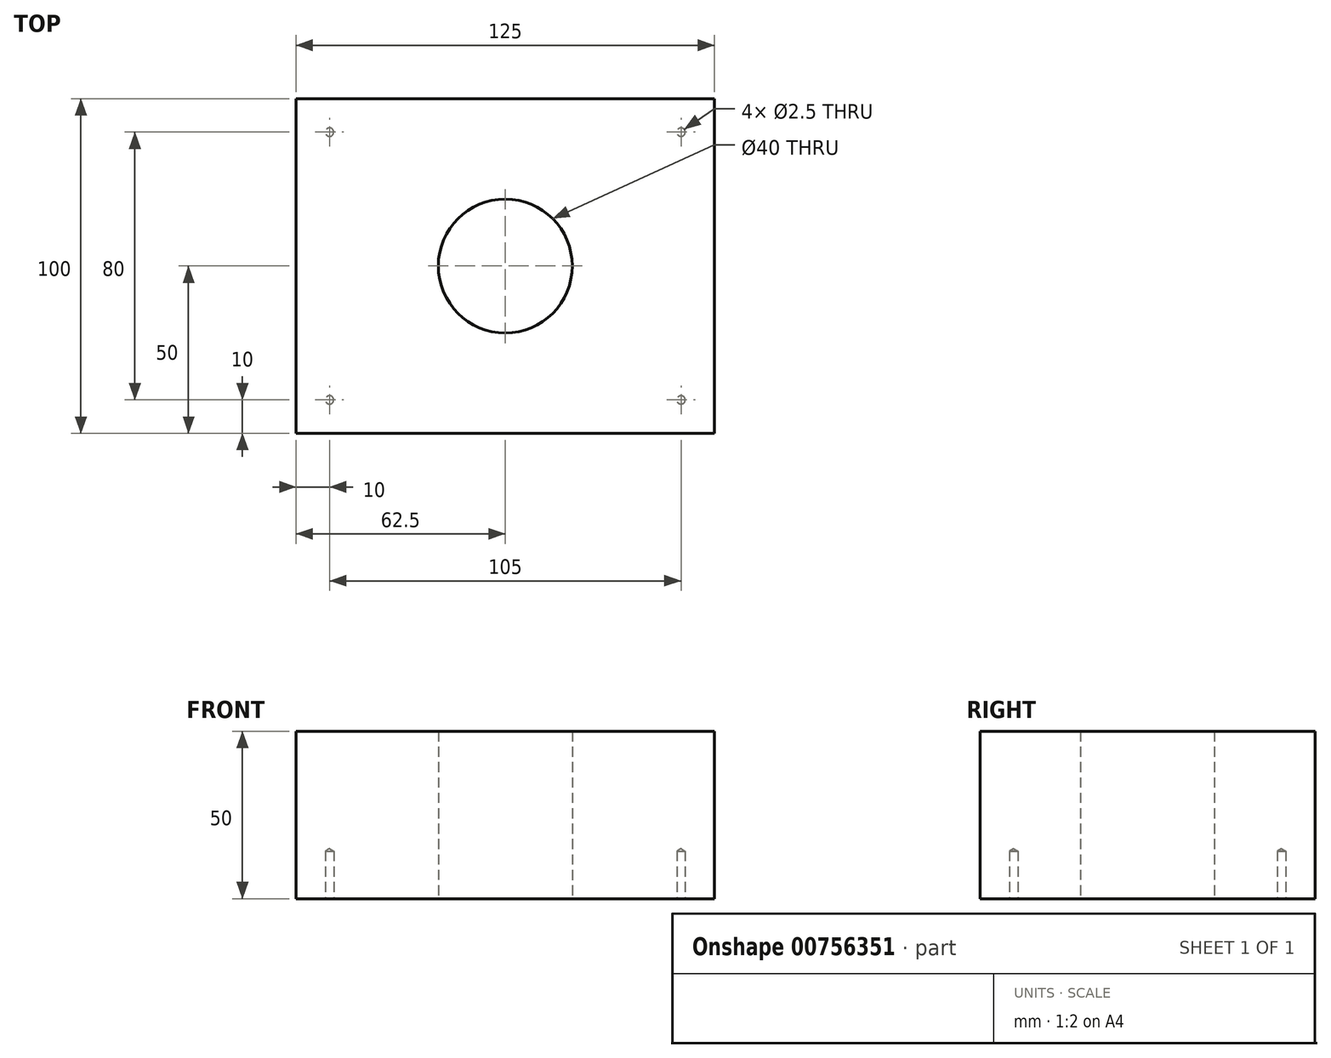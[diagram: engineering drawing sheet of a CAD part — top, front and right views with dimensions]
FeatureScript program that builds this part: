
annotation { "Feature Type Name" : "Feature", "Feature Type Description" : "" }
export const myFeature = defineFeature(function(context is Context, id is Id, definition is map)
    precondition{}
    {
        {
            var Q0;
            Q0=qCreatedBy(makeId("Top.planeOp"),FACE);
            var sketch = newSketch(context, id + "F0", { "sketchPlane" : qUnion([Q0])});
            skLineSegment(sketch, "E0.bottom", {"start": v(62.5, 50) * mm, "end": v(-62.5, 50) * mm});
            skLineSegment(sketch, "E0.top", {"start": v(62.5, -50) * mm, "end": v(-62.5, -50) * mm});
            skLineSegment(sketch, "E0.left", {"start": v(62.5, 50) * mm, "end": v(62.5, -50) * mm});
            skLineSegment(sketch, "E0.right", {"start": v(-62.5, 50) * mm, "end": v(-62.5, -50) * mm});
            skPoint(sketch, "E0.middle", {"position": v(0, 0) * mm});
            skCircle(sketch, "E1", {"center": v(0, 0) * mm, "radius": 20 * mm});
            skSolve(sketch);
        }
        {
            var Q0;
            Q0=makeQuery(id+"F0.imprint","IMPRINT",FACE,{"disambiguationData":[TD([[makeQuery(id+"F0.imprint","IMPRINT",EDGE,{"derivedFrom":sQuery(id+"F0.wireOp",EDGE,"E0.bottom")}),1.0]])]});
            extrude(context, id + "F1", {"entities" : qUnion([Q0]), "depth" : 50 * mm, "offsetDistance" : 25.4 * mm});
        }
        {
            var Q0;
            Q0=makeQuery(id+"F1.opExtrude","CAP_FACE",FACE,{"disambiguationData":[OSD([sQuery(id+"F0.wireOp",EDGE,"E0.bottom"),sQuery(id+"F0.wireOp",EDGE,"E0.top"),sQuery(id+"F0.wireOp",EDGE,"E0.left"),sQuery(id+"F0.wireOp",EDGE,"E0.right"),sQuery(id+"F0.wireOp",EDGE,"E1")])],"isStart":true});
            var sketch = newSketch(context, id + "F2", { "sketchPlane" : qUnion([Q0])});
            skPoint(sketch, "E2", {"position": v(-52.5, 40) * mm});
            skPoint(sketch, "E3", {"position": v(-52.5, -40) * mm});
            skLineSegment(sketch, "E4", {"start": v(0, 50) * mm, "end": v(0, -50) * mm, "construction": true});
            skPoint(sketch, "E5.MirrorP", {"position": v(52.5, 40) * mm});
            skPoint(sketch, "E6.MirrorP", {"position": v(52.5, -40) * mm});
            skSolve(sketch);
        }
        {
            var Q0;
            Q0=sQuery(id+"F2.wireOp",VERTEX,"E3");
            var Q1;
            Q1=sQuery(id+"F2.wireOp",VERTEX,"E2");
            var Q2;
            Q2=sQuery(id+"F2.wireOp",VERTEX,"E5.MirrorP");
            var Q3;
            Q3=sQuery(id+"F2.wireOp",VERTEX,"E6.MirrorP");
            var Q4;
            Q4=makeQuery(id+"F1.opExtrude","SWEPT_BODY",BODY,{"disambiguationData":[OSD([sQuery(id+"F0.wireOp",EDGE,"E0.bottom"),sQuery(id+"F0.wireOp",EDGE,"E0.top"),sQuery(id+"F0.wireOp",EDGE,"E0.left"),sQuery(id+"F0.wireOp",EDGE,"E0.right"),sQuery(id+"F0.wireOp",EDGE,"E1")])]});
            hole(context, id + "F3", {"style" : HoleStyle.SIMPLE, "endStyle" : HoleEndStyle.BLIND, "standardTappedOrClearance" : lookupTablePath({ "standard" : "ISO", "engagement" : "75%", "pitch" : "0.5 mm", "size" : "M3", "type" : "Tapped" }), "standardBlindInLast" : lookupTablePath({ "standard" : "ISO", "engagement" : "75%", "pitch" : "0.5 mm", "size" : "M3", "type" : "Tapped" }), "holeDiameter" : 2.5 * mm, "majorDiameter" : 3 * mm, "showTappedDepth" : true, "holeDepth" : 14.2 * mm, "isTappedThrough" : true, "tappedDepth" : 12.7 * mm, "tapClearance" : 3, "locations" : qUnion([Q0, Q1, Q2, Q3]), "scope" : qUnion([Q4])});
        }
    });
